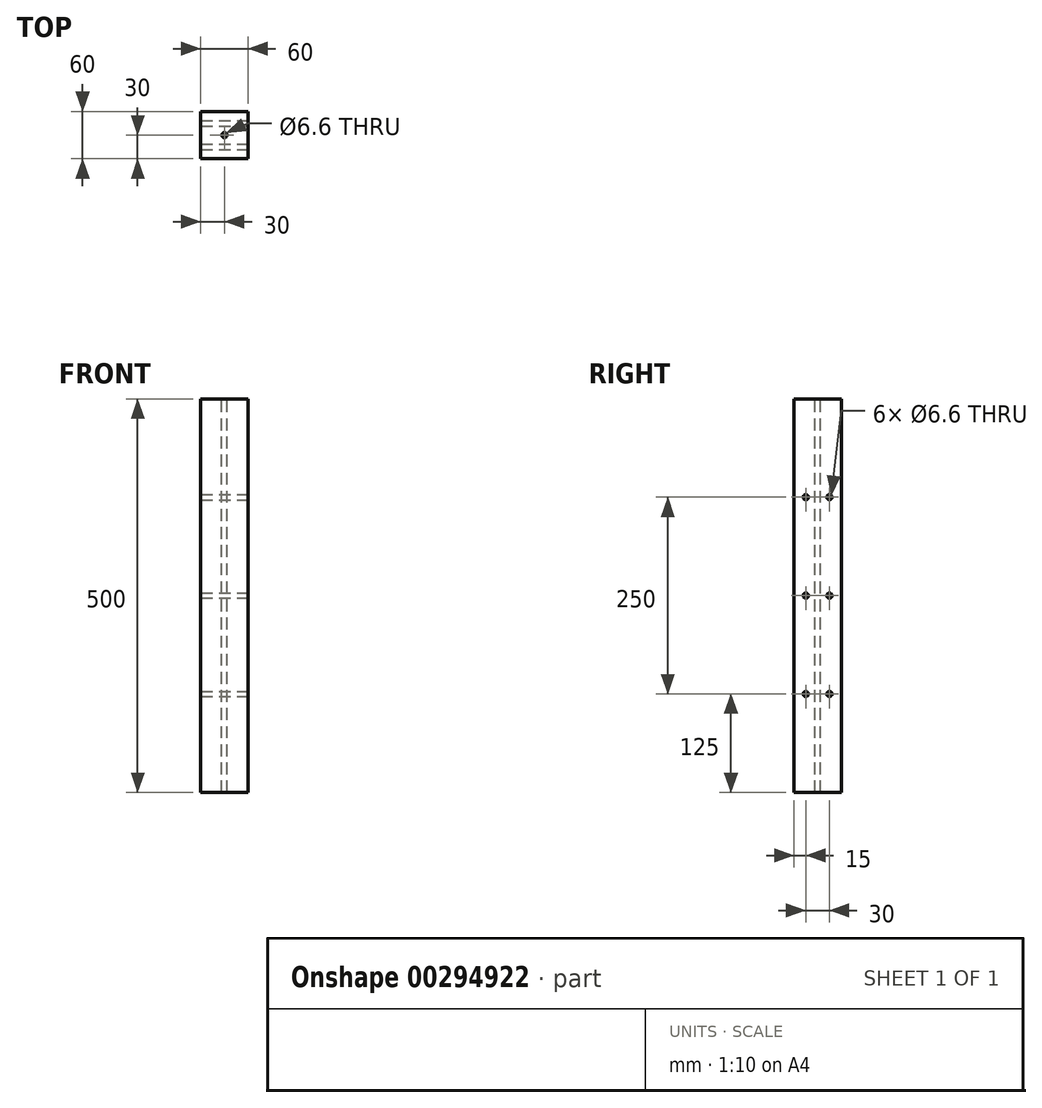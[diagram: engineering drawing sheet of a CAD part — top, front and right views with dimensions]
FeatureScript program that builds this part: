
annotation { "Feature Type Name" : "Feature", "Feature Type Description" : "" }
export const myFeature = defineFeature(function(context is Context, id is Id, definition is map)
    precondition{}
    {
        {
            var Q0;
            Q0=qCreatedBy(makeId("Top.planeOp"),FACE);
            var sketch = newSketch(context, id + "F0", { "sketchPlane" : qUnion([Q0])});
            skLineSegment(sketch, "E0.bottom", {"start": v(-30, 30) * mm, "end": v(30, 30) * mm});
            skLineSegment(sketch, "E0.top", {"start": v(-30, -30) * mm, "end": v(30, -30) * mm});
            skLineSegment(sketch, "E0.left", {"start": v(-30, 30) * mm, "end": v(-30, -30) * mm});
            skLineSegment(sketch, "E0.right", {"start": v(30, 30) * mm, "end": v(30, -30) * mm});
            skPoint(sketch, "E0.middle", {"position": v(0, 0) * mm});
            skSolve(sketch);
        }
        {
            var Q0;
            Q0=makeQuery(id+"F0.imprint","IMPRINT",FACE,{"disambiguationData":[TD([[makeQuery(id+"F0.imprint","IMPRINT",EDGE,{"derivedFrom":sQuery(id+"F0.wireOp",EDGE,"E0.bottom")}),-1.0]])]});
            extrude(context, id + "F1", {"entities" : qUnion([Q0]), "depth" : 500 * mm, "offsetDistance" : 25 * mm});
        }
        {
            var Q0;
            Q0=makeQuery(id+"F1.opExtrude","CAP_FACE",FACE,{"disambiguationData":[OSD([sQuery(id+"F0.wireOp",EDGE,"E0.bottom"),sQuery(id+"F0.wireOp",EDGE,"E0.top"),sQuery(id+"F0.wireOp",EDGE,"E0.left"),sQuery(id+"F0.wireOp",EDGE,"E0.right")])],"isStart":false});
            var sketch = newSketch(context, id + "F2", { "sketchPlane" : qUnion([Q0])});
            skPoint(sketch, "E1", {"position": v(0, 0) * mm});
            skSolve(sketch);
        }
        {
            var Q0;
            Q0=sQuery(id+"F2.wireOp",VERTEX,"E1");
            var Q1;
            Q1=makeQuery(id+"F1.opExtrude","SWEPT_BODY",BODY,{"disambiguationData":[OSD([sQuery(id+"F0.wireOp",EDGE,"E0.bottom"),sQuery(id+"F0.wireOp",EDGE,"E0.top"),sQuery(id+"F0.wireOp",EDGE,"E0.left"),sQuery(id+"F0.wireOp",EDGE,"E0.right")])]});
            hole(context, id + "F3", {"style" : HoleStyle.SIMPLE, "endStyle" : HoleEndStyle.THROUGH, "standardTappedOrClearance" : lookupTablePath({ "standard" : "ISO", "fit" : "Normal", "size" : "M6", "type" : "Clearance" }), "standardBlindInLast" : lookupTablePath({ "fit" : "Standard", "standard" : "ISO", "size" : "M6", "type" : "Clearance" }), "holeDiameter" : 6.6 * mm, "isTappedThrough" : true, "tappedDepth" : 12 * mm, "tapClearance" : 3, "locations" : qUnion([Q0]), "scope" : qUnion([Q1])});
        }
        {
            var Q0;
            Q0=makeQuery(id+"F1.opExtrude","SWEPT_FACE",FACE,{"disambiguationData":[OSD([sQuery(id+"F0.wireOp",EDGE,"E0.right")])]});
            var sketch = newSketch(context, id + "F4", { "sketchPlane" : qUnion([Q0])});
            skLineSegment(sketch, "E2", {"start": v(0, 0) * mm, "end": v(0, 500) * mm, "construction": true});
            skLineSegment(sketch, "E3", {"start": v(0, 0) * mm, "end": v(30, 0) * mm, "construction": true});
            skLineSegment(sketch, "E4", {"start": v(0, 0) * mm, "end": v(-30, 0) * mm, "construction": true});
            skLineSegment(sketch, "E5", {"start": v(-15, 0) * mm, "end": v(-15, 500) * mm, "construction": true});
            skLineSegment(sketch, "E6", {"start": v(15, 0) * mm, "end": v(15, 500) * mm, "construction": true});
            skPoint(sketch, "E7", {"position": v(15, 125) * mm});
            skPoint(sketch, "E8", {"position": v(15, 250) * mm});
            skPoint(sketch, "E9", {"position": v(15, 375) * mm});
            skPoint(sketch, "E10", {"position": v(-15, 125) * mm});
            skPoint(sketch, "E11", {"position": v(-15, 250) * mm});
            skPoint(sketch, "E12", {"position": v(-15, 375) * mm});
            skSolve(sketch);
        }
        {
            var Q0;
            Q0=sQuery(id+"F4.wireOp",VERTEX,"E12");
            var Q1;
            Q1=sQuery(id+"F4.wireOp",VERTEX,"E9");
            var Q2;
            Q2=sQuery(id+"F4.wireOp",VERTEX,"E8");
            var Q3;
            Q3=sQuery(id+"F4.wireOp",VERTEX,"E7");
            var Q4;
            Q4=sQuery(id+"F4.wireOp",VERTEX,"E10");
            var Q5;
            Q5=sQuery(id+"F4.wireOp",VERTEX,"E11");
            var Q6;
            Q6=makeQuery(id+"F1.opExtrude","SWEPT_BODY",BODY,{"disambiguationData":[OSD([sQuery(id+"F0.wireOp",EDGE,"E0.bottom"),sQuery(id+"F0.wireOp",EDGE,"E0.top"),sQuery(id+"F0.wireOp",EDGE,"E0.left"),sQuery(id+"F0.wireOp",EDGE,"E0.right")])]});
            hole(context, id + "F5", {"style" : HoleStyle.SIMPLE, "endStyle" : HoleEndStyle.THROUGH, "standardTappedOrClearance" : lookupTablePath({ "standard" : "ISO", "fit" : "Normal", "size" : "M6", "type" : "Clearance" }), "standardBlindInLast" : lookupTablePath({ "fit" : "Standard", "standard" : "ISO", "size" : "M6", "type" : "Clearance" }), "holeDiameter" : 6.6 * mm, "isTappedThrough" : true, "tappedDepth" : 12 * mm, "tapClearance" : 3, "locations" : qUnion([Q0, Q1, Q2, Q3, Q4, Q5]), "scope" : qUnion([Q6])});
        }
    });
